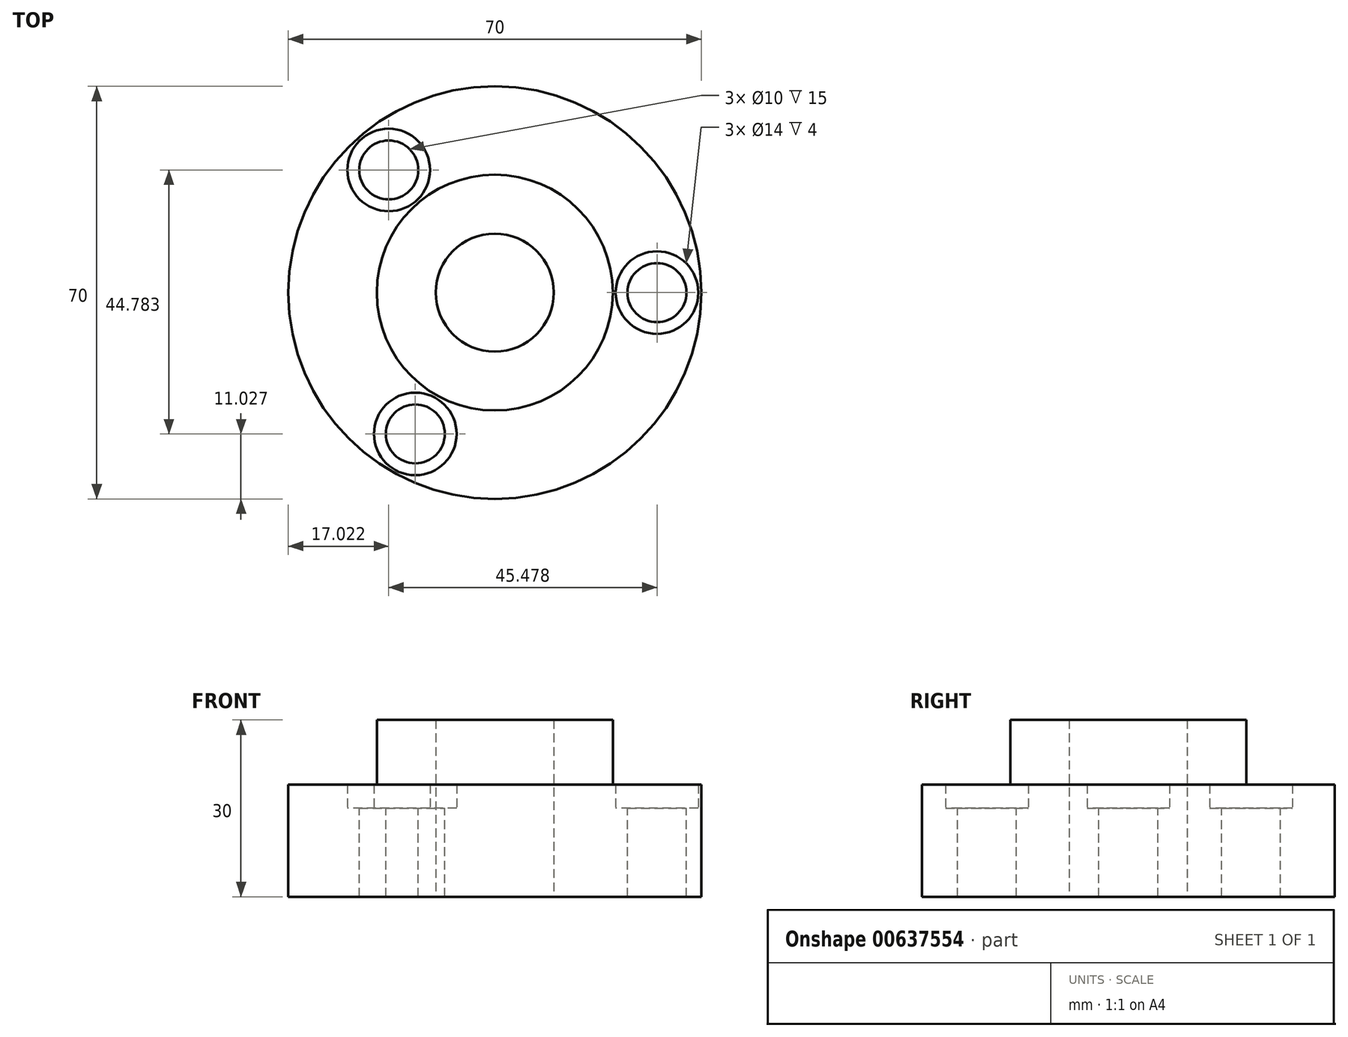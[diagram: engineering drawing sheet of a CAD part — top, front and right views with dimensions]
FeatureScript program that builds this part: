
annotation { "Feature Type Name" : "Feature", "Feature Type Description" : "" }
export const myFeature = defineFeature(function(context is Context, id is Id, definition is map)
    precondition{}
    {
        {
            var Q0;
            Q0=qCreatedBy(makeId("Top.planeOp"),FACE);
            var sketch = newSketch(context, id + "F0", { "sketchPlane" : qUnion([Q0])});
            skCircle(sketch, "E0", {"center": v(0, 0) * mm, "radius": 10 * mm});
            skCircle(sketch, "E1", {"center": v(0, 0) * mm, "radius": 20 * mm});
            skSolve(sketch);
        }
        {
            var Q0;
            Q0=makeQuery(id+"F0.imprint","IMPRINT",FACE,{"disambiguationData":[TD([[makeQuery(id+"F0.imprint","IMPRINT",EDGE,{"derivedFrom":sQuery(id+"F0.wireOp",EDGE,"E0")}),-1.0]])]});
            extrude(context, id + "F1", {"entities" : qUnion([Q0]), "depth" : 15 * mm, "offsetDistance" : 25 * mm});
        }
        {
            var Q0;
            Q0=makeQuery(id+"F1.opExtrude","CAP_FACE",FACE,{"disambiguationData":[OSD([sQuery(id+"F0.wireOp",EDGE,"E0"),sQuery(id+"F0.wireOp",EDGE,"E1")])],"isStart":true});
            var sketch = newSketch(context, id + "F2", { "sketchPlane" : qUnion([Q0])});
            skCircle(sketch, "E2", {"center": v(0, 0) * mm, "radius": 10 * mm});
            skCircle(sketch, "E3", {"center": v(0, 0) * mm, "radius": 35 * mm});
            skCircle(sketch, "E4", {"center": v(-17.98, -20.81) * mm, "radius": 5 * mm});
            skCircle(sketch, "E5", {"center": v(-13.47, 23.97) * mm, "radius": 5 * mm});
            skCircle(sketch, "E6", {"center": v(27.5, 0) * mm, "radius": 5 * mm});
            skSolve(sketch);
        }
        {
            var Q0;
            Q0 = qSketchRegion(id + "F2", true);
            extrude(context, id + "F3", {"entities" : qUnion([Q0]), "operationType" : NewBodyOperationType.ADD, "depth" : 15 * mm, "offsetDistance" : 25 * mm});
        }
        {
            var Q0;
            Q0=makeQuery(id+"F3.opExtrude","CAP_FACE",FACE,{"disambiguationData":[OSD([sQuery(id+"F2.wireOp",EDGE,"E2"),sQuery(id+"F2.wireOp",EDGE,"E3"),sQuery(id+"F2.wireOp",EDGE,"E4"),sQuery(id+"F2.wireOp",EDGE,"E5"),sQuery(id+"F2.wireOp",EDGE,"E6")])],"isStart":true});
            var sketch = newSketch(context, id + "F4", { "sketchPlane" : qUnion([Q0])});
            skCircle(sketch, "E7", {"center": v(0, 0) * mm, "radius": 35 * mm});
            skCircle(sketch, "E8", {"center": v(0, 0) * mm, "radius": 20 * mm});
            skCircle(sketch, "E9", {"center": v(-17.98, 20.81) * mm, "radius": 7 * mm});
            skCircle(sketch, "E10", {"center": v(27.5, 0) * mm, "radius": 7 * mm});
            skCircle(sketch, "E11", {"center": v(-13.47, -23.97) * mm, "radius": 7 * mm});
            skSolve(sketch);
        }
        {
            var Q0;
            Q0 = qSketchRegion(id + "F4", true);
            extrude(context, id + "F5", {"entities" : qUnion([Q0]), "operationType" : NewBodyOperationType.ADD, "depth" : 4 * mm, "offsetDistance" : 25 * mm});
        }
    });
